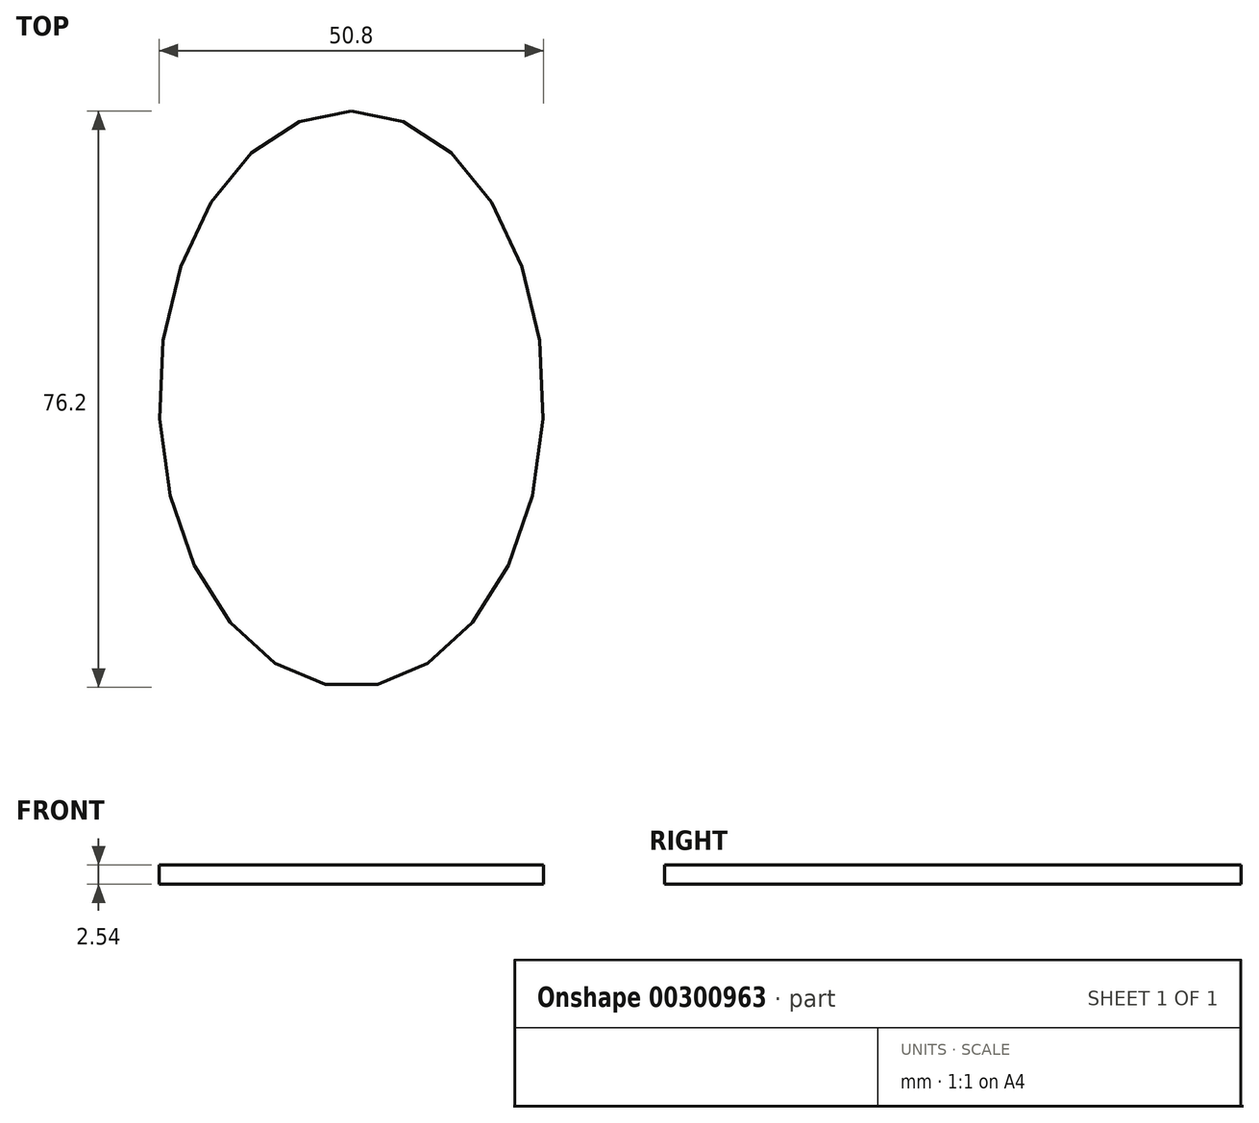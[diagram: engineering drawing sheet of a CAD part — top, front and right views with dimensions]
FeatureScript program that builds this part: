
annotation { "Feature Type Name" : "Feature", "Feature Type Description" : "" }
export const myFeature = defineFeature(function(context is Context, id is Id, definition is map)
    precondition{}
    {
        {
            var Q0;
            Q0=qCreatedBy(makeId("Top.planeOp"),FACE);
            var sketch = newSketch(context, id + "F0", { "sketchPlane" : qUnion([Q0])});
            skEllipse(sketch, "E0", {"center": v(0, 0) * mm, "majorRadius": 38.1 * mm, "minorRadius": 25.4 * mm, "majorAxis": v(0, 1)});
            skSolve(sketch);
        }
        {
            var Q0;
            Q0=makeQuery(id+"F0.imprint","IMPRINT",FACE,{"disambiguationData":[TD([[makeQuery(id+"F0.imprint","IMPRINT",EDGE,{"derivedFrom":sQuery(id+"F0.wireOp",EDGE,"E0")}),1.0]])]});
            extrude(context, id + "F1", {"entities" : qUnion([Q0]), "depth" : 2.54 * mm});
        }
    });
